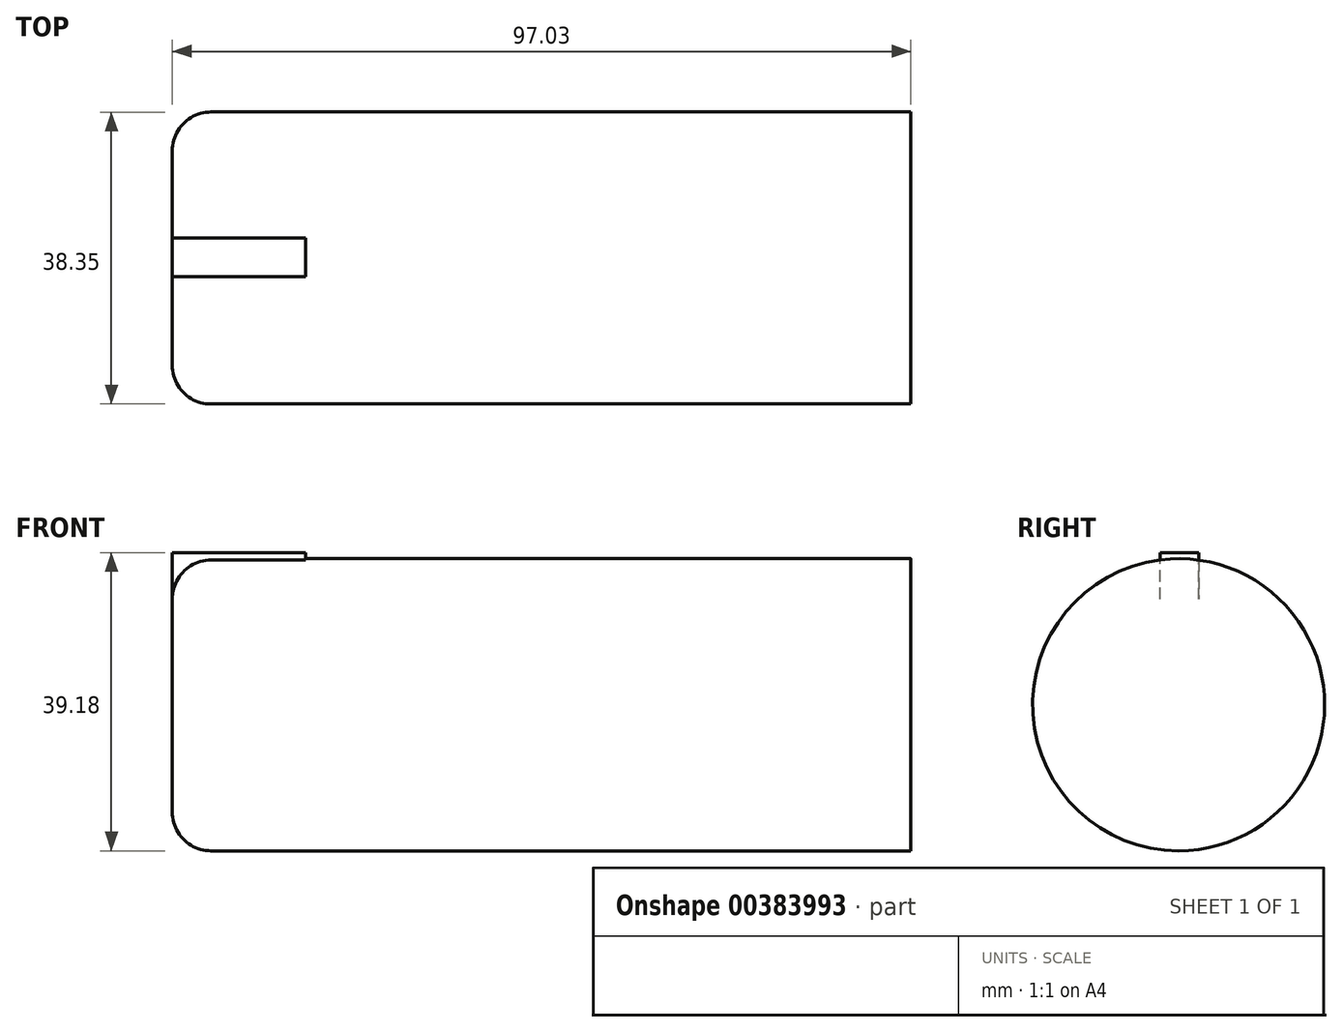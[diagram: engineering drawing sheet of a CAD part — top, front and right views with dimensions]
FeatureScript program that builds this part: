
annotation { "Feature Type Name" : "Feature", "Feature Type Description" : "" }
export const myFeature = defineFeature(function(context is Context, id is Id, definition is map)
    precondition{}
    {
        {
            var Q0;
            Q0=qCreatedBy(makeId("Right.planeOp"),FACE);
            var sketch = newSketch(context, id + "F0", { "sketchPlane" : qUnion([Q0])});
            skCircle(sketch, "E0", {"center": v(2.45, 0) * mm, "radius": 19.18 * mm});
            skSolve(sketch);
        }
        {
            var Q0;
            Q0=makeQuery(id+"F0.imprint","IMPRINT",FACE,{"disambiguationData":[TD([[makeQuery(id+"F0.imprint","IMPRINT",EDGE,{"derivedFrom":sQuery(id+"F0.wireOp",EDGE,"E0")}),1.0]])]});
            extrude(context, id + "F1", {"entities" : qUnion([Q0]), "depth" : 97.03 * mm, "offsetDistance" : 25.4 * mm});
        }
        {
            var Q0;
            Q0=qCreatedBy(makeId("Front.planeOp"),FACE);
            var sketch = newSketch(context, id + "F2", { "sketchPlane" : qUnion([Q0])});
            skLineSegment(sketch, "E1", {"start": v(0, 20) * mm, "end": v(17.52, 20) * mm});
            skLineSegment(sketch, "E2", {"start": v(17.52, 16.04) * mm, "end": v(0, 16.04) * mm});
            skLineSegment(sketch, "E3", {"start": v(0, 16.04) * mm, "end": v(0, 20) * mm});
            skLineSegment(sketch, "E4", {"start": v(17.52, 20) * mm, "end": v(17.52, 16.04) * mm});
            skLineSegment(sketch, "E5", {"start": v(0, 0) * mm, "end": v(8.76, 0) * mm});
            skPoint(sketch, "E5.endSnap0", {"position": v(8.76, 16.04) * mm});
            skLineSegment(sketch, "E6", {"start": v(8.76, 0) * mm, "end": v(4, 331.63) * mm});
            skSolve(sketch);
        }
        {
            var Q0;
            Q0 = qSketchRegion(id + "F2", true);
            extrude(context, id + "F3", {"entities" : qUnion([Q0]), "operationType" : NewBodyOperationType.ADD, "oppositeDirection" : true, "depth" : 5.08 * mm, "offsetDistance" : 25.4 * mm});
        }
        {
            var Q0;
            Q0=makeQuery(id+"F1.opExtrude","CAP_EDGE",EDGE,{"disambiguationData":[OSD([sQuery(id+"F0.wireOp",EDGE,"E0")])],"isStart":true});
            fillet(context, id + "F4", {"entities" : qUnion([Q0]), "radius" : 5.08 * mm, "tangentPropagation" : true, "allowEdgeOverflow" : false});
        }
    });
